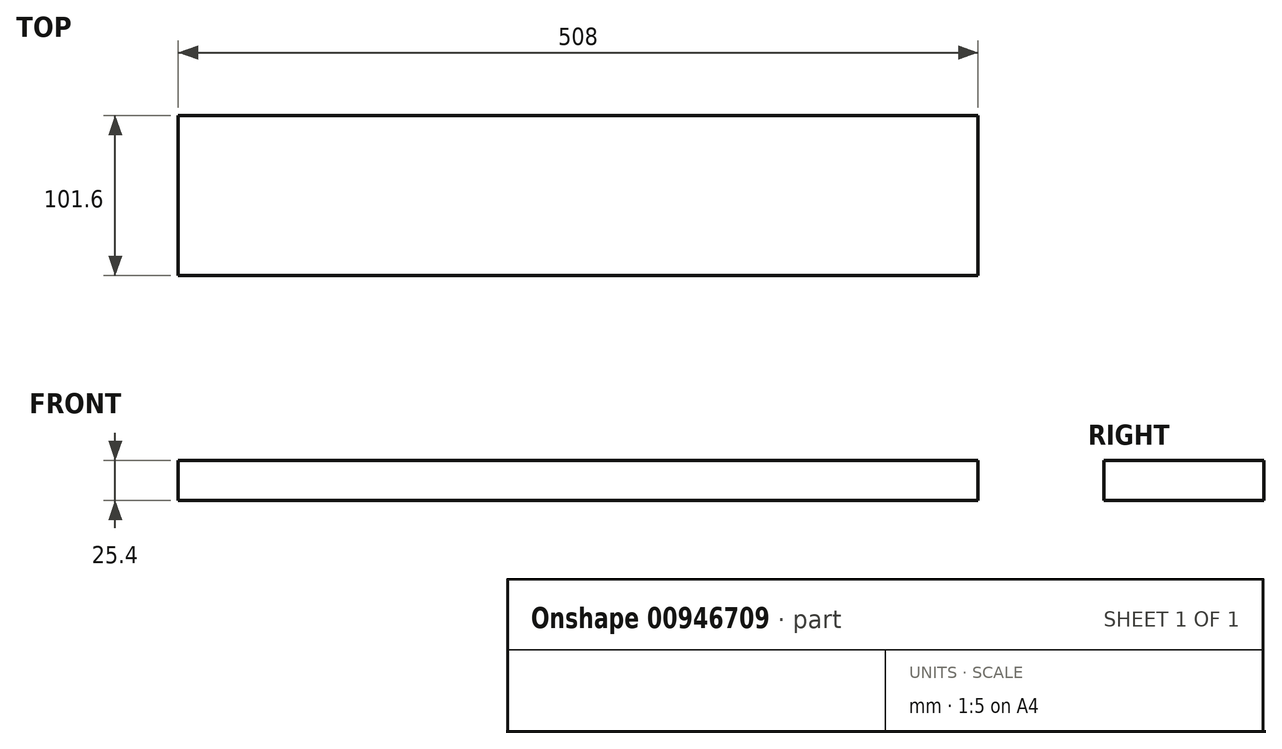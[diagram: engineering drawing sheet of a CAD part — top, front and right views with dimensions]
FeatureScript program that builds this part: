
annotation { "Feature Type Name" : "Feature", "Feature Type Description" : "" }
export const myFeature = defineFeature(function(context is Context, id is Id, definition is map)
    precondition{}
    {
        {
            var Q0;
            Q0=qCreatedBy(makeId("Top.planeOp"),FACE);
            var sketch = newSketch(context, id + "F0", { "sketchPlane" : qUnion([Q0])});
            skLineSegment(sketch, "E0.bottom", {"start": v(254, 50.8) * mm, "end": v(-254, 50.8) * mm});
            skLineSegment(sketch, "E0.top", {"start": v(254, -50.8) * mm, "end": v(-254, -50.8) * mm});
            skLineSegment(sketch, "E0.left", {"start": v(254, 50.8) * mm, "end": v(254, -50.8) * mm});
            skLineSegment(sketch, "E0.right", {"start": v(-254, 50.8) * mm, "end": v(-254, -50.8) * mm});
            skPoint(sketch, "E0.middle", {"position": v(0, 0) * mm});
            skSolve(sketch);
        }
        {
            var Q0;
            Q0=qSketchRegion(id+"F0",true);
            extrude(context, id + "F1", {"entities" : qUnion([Q0]), "depth" : 25.4 * mm, "offsetDistance" : 25.4 * mm});
        }
    });
